# Revit family: VRB_Bollard
name_source: partatom
category: Lighting Fixtures
units: mm (PartAtom-declared; Revit-internal decimal feet)

## family parameters
Always vertical = Yes
Cut with Voids When Loaded = No
Light Source = Yes
OmniClass Number = 23.80.70.14
OmniClass Title = Luminaries for External Lighting
Part Type = Normal
Room Calculation Point = No
Round Connector Dimension = Use Diameter
Shared = No
Work Plane-Based = No

## types (1)
- VRB
    Apparent Load = 0 VA
    Assembly Code = D5020200
    Color Filter = 16777215
    Default Elevation = 0' - 0"
    Description = Low Level Luminaire
    Diameter = 0' - 8"
    Dimming Lamp Color Temperature Shift = <None>
    Finish = Powder Coat-Dark Bronze
    Glass = Glass-Temper Molded
    Height = 3' - 6"
    Lamp = LED
    Load Classification = Lighting
    Manufacturer = Kim Lighting
    MasterFormat Title = Landscape Lighting, Site Lighting, Walkway Lighting
    Model = VRB Bollard
    Note Text = LF
    Note Visible = Yes
    Number of Poles = 1
    Photometric Notes = More IES files download on Photometric Web Link
    Photometric Web File = vrb1-10l4k.ies
    Power Factor = 1
    Radius = 0' - 4"
    Series = Vandal-Resistant Bollards
    Tilt Angle = 90.00°
    Type Comments = Lighted Bollard
    URL = https://www.currentlighting.com
    Voltage = 120 V
    Wattage Comments = default

## geometry (parser evidence)
native form markers: Sweep x2
no freeform markers — native parametric forms only
